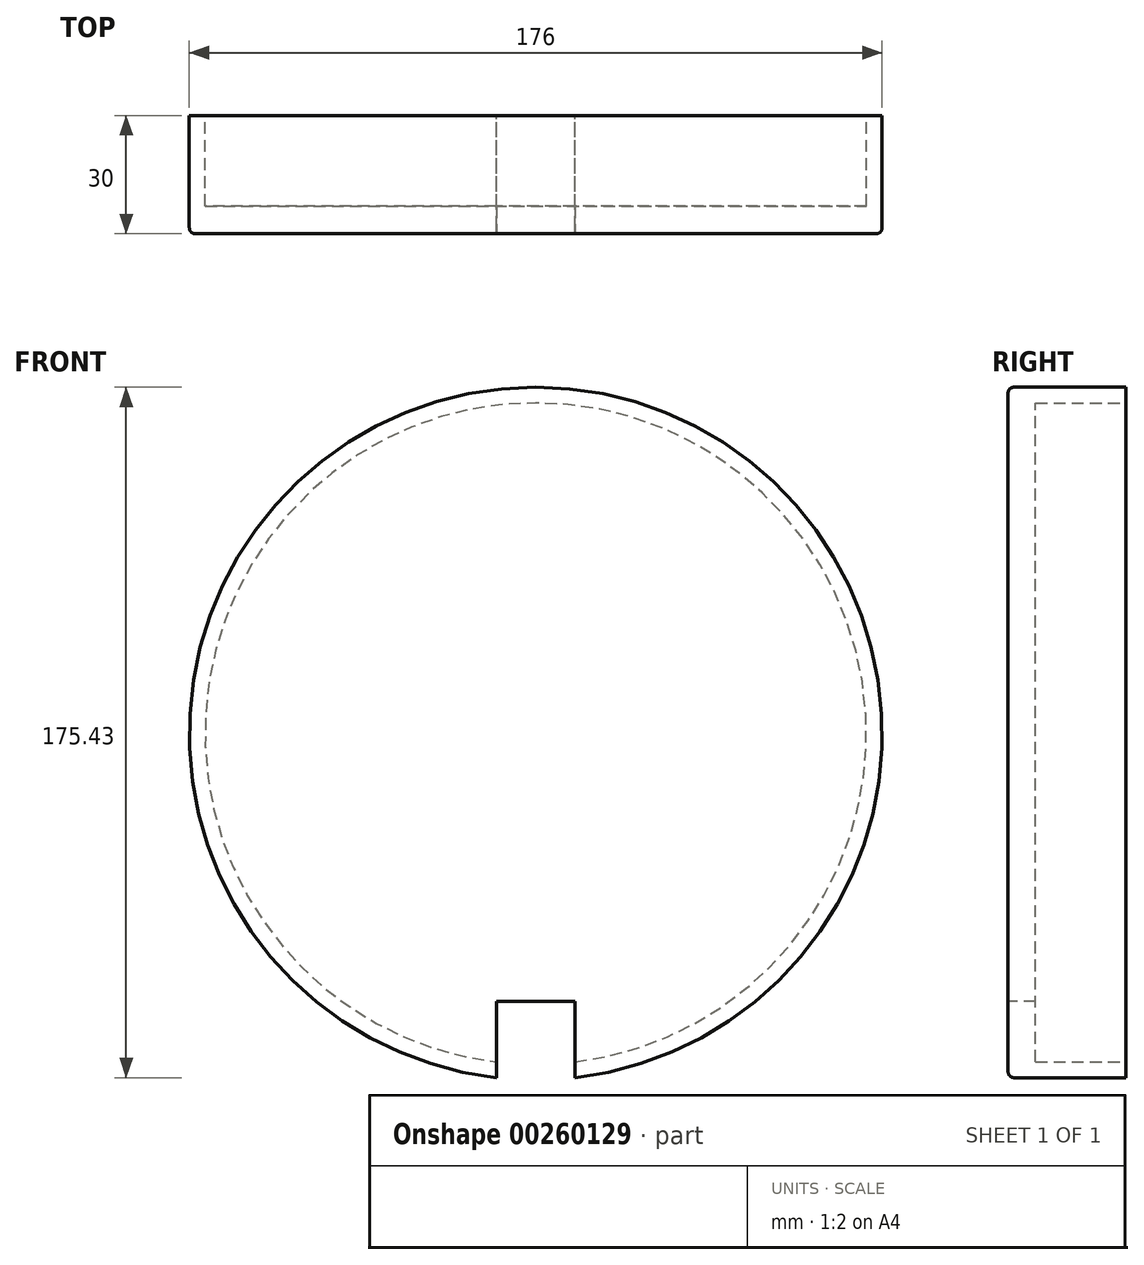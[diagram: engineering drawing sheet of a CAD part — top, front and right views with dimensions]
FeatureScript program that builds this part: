
annotation { "Feature Type Name" : "Feature", "Feature Type Description" : "" }
export const myFeature = defineFeature(function(context is Context, id is Id, definition is map)
    precondition{}
    {
        {
            var Q0;
            Q0=qCreatedBy(makeId("Front.planeOp"),FACE);
            var sketch = newSketch(context, id + "F0", { "sketchPlane" : qUnion([Q0])});
            skCircle(sketch, "E0", {"center": v(0, 0) * mm, "radius": 88 * mm});
            skSolve(sketch);
        }
        {
            var Q0;
            Q0=makeQuery(id+"F0.imprint","IMPRINT",FACE,{"disambiguationData":[TD([[makeQuery(id+"F0.imprint","IMPRINT",EDGE,{"derivedFrom":sQuery(id+"F0.wireOp",EDGE,"E0")}),1.0]])]});
            var Q1;
            Q1=sQuery(id+"F0.wireOp",EDGE,"E0");
            extrude(context, id + "F1", {"entities" : qUnion([Q0]), "surfaceEntities" : qUnion([Q1]), "depth" : 30 * mm});
        }
        {
            var Q0;
            Q0=makeQuery(id+"F1.opExtrude","CAP_FACE",FACE,{"disambiguationData":[OSD([sQuery(id+"F0.wireOp",EDGE,"E0")])],"isStart":true});
            var sketch = newSketch(context, id + "F2", { "sketchPlane" : qUnion([Q0])});
            skCircle(sketch, "E1", {"center": v(0, 0) * mm, "radius": 84 * mm});
            skSolve(sketch);
        }
        {
            var Q0;
            Q0=qSketchRegion(id+"F2",true);
            var Q1;
            Q1=qSketchRegion(id+"F9u2Kz7b36xQZs2_1",true);
            extrude(context, id + "F3", {"entities" : qUnion([Q0, Q1]), "operationType" : NewBodyOperationType.REMOVE, "oppositeDirection" : true, "depth" : 23 * mm});
        }
        {
            var Q0;
            Q0=makeQuery(id+"F1.opExtrude","CAP_EDGE",EDGE,{"disambiguationData":[OSD([sQuery(id+"F0.wireOp",EDGE,"E0")])],"isStart":false});
            fillet(context, id + "F4", {"entities" : qUnion([Q0]), "radius" : 1.5 * mm, "tangentPropagation" : true, "allowEdgeOverflow" : false});
        }
        {
            var Q0;
            Q0=makeQuery(id+"F1.opExtrude","CAP_FACE",FACE,{"disambiguationData":[OSD([sQuery(id+"F0.wireOp",EDGE,"E0")])],"isStart":false});
            var sketch = newSketch(context, id + "F5", { "sketchPlane" : qUnion([Q0])});
            skLineSegment(sketch, "E2.bottom", {"start": v(-10, -68) * mm, "end": v(10, -68) * mm});
            skLineSegment(sketch, "E2.top", {"start": v(-10, -88) * mm, "end": v(10, -88) * mm});
            skLineSegment(sketch, "E2.left", {"start": v(-10, -68) * mm, "end": v(-10, -88) * mm});
            skLineSegment(sketch, "E2.right", {"start": v(10, -68) * mm, "end": v(10, -88) * mm});
            skSolve(sketch);
        }
        {
            var Q0;
            Q0=qSketchRegion(id+"F5",true);
            extrude(context, id + "F6", {"entities" : qUnion([Q0]), "operationType" : NewBodyOperationType.REMOVE, "endBound" : BoundingType.THROUGH_ALL, "oppositeDirection" : true, "depth" : 40 * mm});
        }
    });
